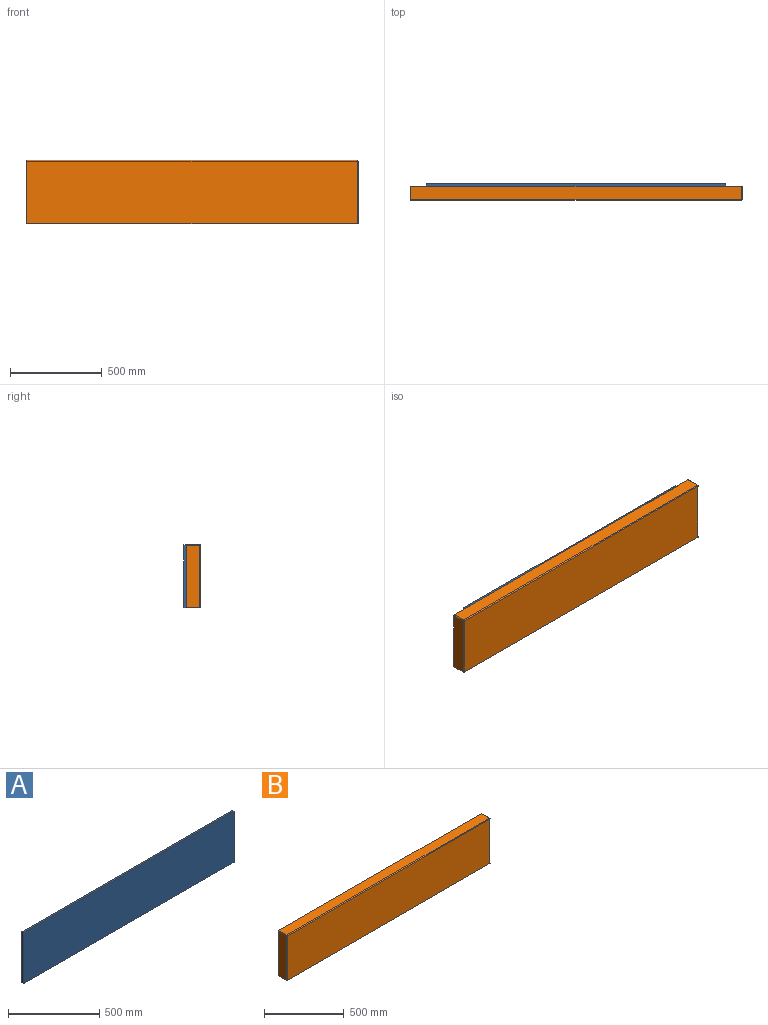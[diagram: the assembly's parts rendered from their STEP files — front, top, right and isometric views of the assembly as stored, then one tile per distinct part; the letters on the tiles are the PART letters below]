
ASSEMBLY  parts=2 mates=1
PART A: 6 faces, bbox 1632x12.7x342.9 mm
  f0: plane 1631.95x12.7mm, normal (0,0,-1), area 20725.8mm2, adj f1,f3,f4,f5
  f1: plane 342.9x12.7mm, normal (1,0,0), area 4354.8mm2, adj f0,f2,f4,f5
  f2: plane 1631.95x12.7mm, normal (0,0,1), area 20725.8mm2, adj f1,f3,f4,f5
  f3: plane 342.9x12.7mm, normal (-1,0,0), area 4354.8mm2, adj f0,f2,f4,f5
  f4: plane 1631.95x342.9mm, normal (0,-1,0), area 559595.7mm2, adj f0,f1,f2,f3
  f5: plane 1631.95x342.9mm, normal (0,1,0), area 559595.7mm2, adj f0,f1,f2,f3
PART B: 13 faces, bbox 1809.8x76.2x345.4 mm
  f0: plane 1809.75x76.2mm, normal (0,0,-1), area 137891.9mm2, adj f1,f3,f4,f5,f6,f9
  f1: plane 340.36x71.12mm, normal (1,0,0), area 24206.4mm2, adj f0,f5,f9,f12
  f2: plane 1799.59x71.12mm, normal (0,0,1), area 127986.8mm2, adj f5,f7,f10,f12
  f3: plane 340.36x71.12mm, normal (-1,0,0), area 24206.4mm2, adj f0,f5,f6,f7
  f4: plane 1799.59x340.36mm, normal (0,-1,0), area 612508.5mm2, adj f0,f6,f9,f10
  f5: plane 1809.75x345.44mm, normal (0,1,0), area 625149mm2, adj f0,f1,f2,f3,f7,f12
  f6: cylinder r=5.08mm len=340.36mm, axis (0,0,1), area 2716mm2, adj f0,f3,f4,f8
  f7: cylinder r=5.08mm len=71.12mm, axis (0,-1,0), area 567.5mm2, adj f2,f3,f5,f8
  f8: sphere r=5.08mm, area 40.5mm2, adj f6,f7,f10
  f9: cylinder r=5.08mm len=340.36mm, axis (0,0,-1), area 2716mm2, adj f0,f1,f4,f11
  f10: cylinder r=5.08mm len=1799.59mm, axis (1,0,0), area 14360.1mm2, adj f2,f4,f8,f11
  f11: sphere r=5.08mm, area 40.5mm2, adj f9,f10,f12
  f12: cylinder r=5.08mm len=71.12mm, axis (0,1,0), area 567.5mm2, adj f1,f2,f5,f11
PLACE A t=(567.43,-351.66,502.29)mm
PLACE B t=(656.33,-364.36,502.29)mm
MATE fastened A.f4 <-> B.f5  axis (0,-1,0) through (-248.55,-364.36,502.29)mm
